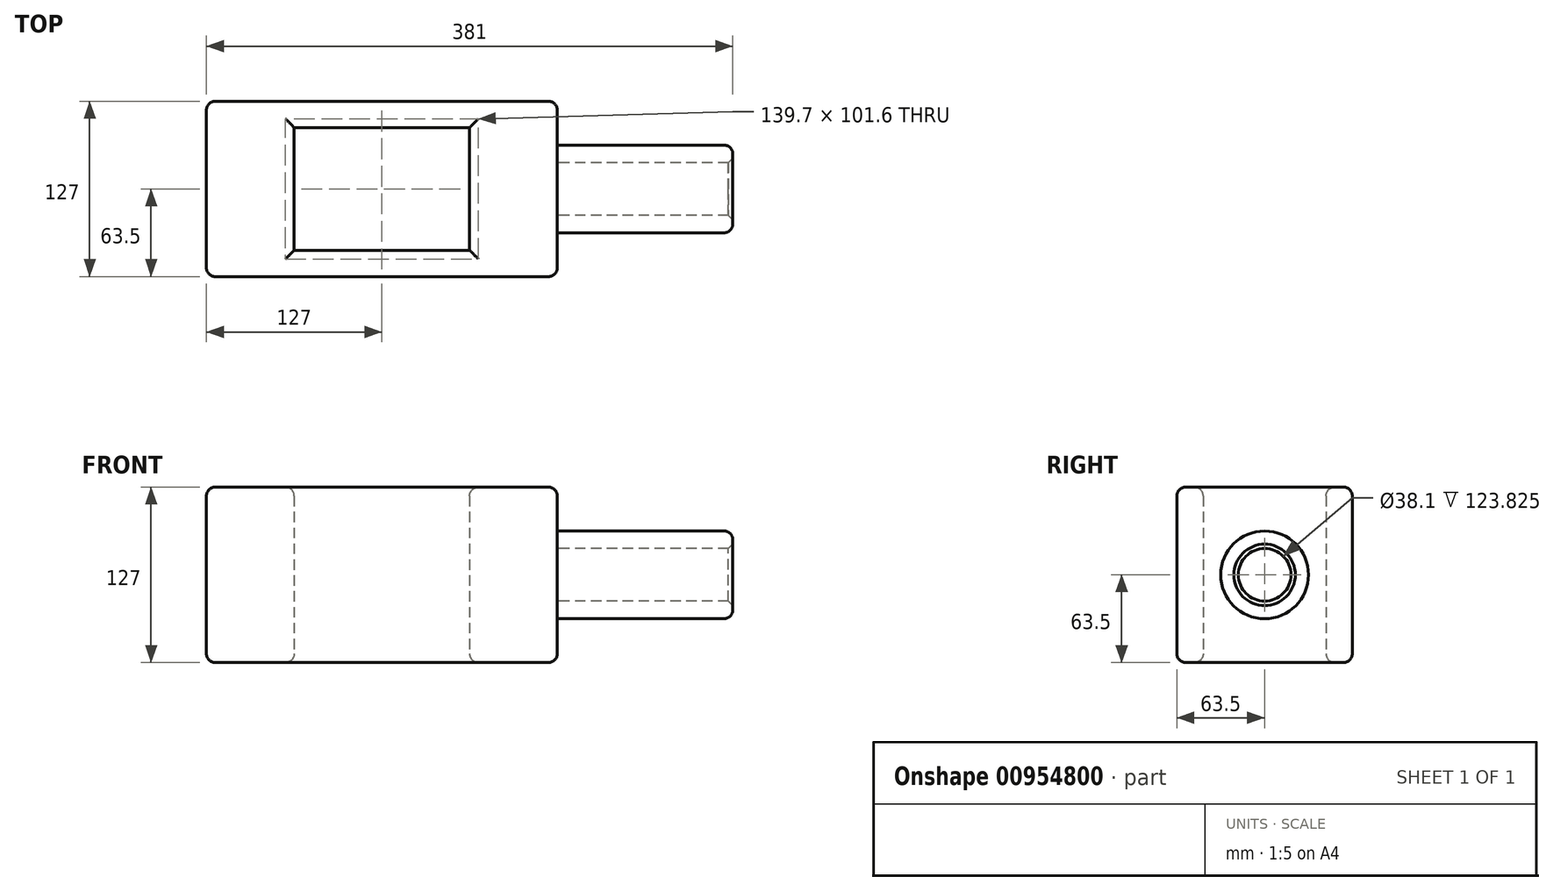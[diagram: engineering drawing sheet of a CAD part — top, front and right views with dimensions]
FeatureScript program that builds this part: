
annotation { "Feature Type Name" : "Feature", "Feature Type Description" : "" }
export const myFeature = defineFeature(function(context is Context, id is Id, definition is map)
    precondition{}
    {
        {
            var Q0;
            Q0=qCreatedBy(makeId("Top.planeOp"),FACE);
            var sketch = newSketch(context, id + "F0", { "sketchPlane" : qUnion([Q0])});
            skLineSegment(sketch, "E0.bottom", {"start": v(127, 63.5) * mm, "end": v(-127, 63.5) * mm});
            skLineSegment(sketch, "E0.top", {"start": v(127, -63.5) * mm, "end": v(-127, -63.5) * mm});
            skLineSegment(sketch, "E0.left", {"start": v(127, 63.5) * mm, "end": v(127, -63.5) * mm});
            skLineSegment(sketch, "E0.right", {"start": v(-127, 63.5) * mm, "end": v(-127, -63.5) * mm});
            skPoint(sketch, "E0.middle", {"position": v(0, 0) * mm});
            skLineSegment(sketch, "E1.bottom", {"start": v(-63.5, -44.45) * mm, "end": v(63.5, -44.45) * mm});
            skLineSegment(sketch, "E1.top", {"start": v(-63.5, 44.45) * mm, "end": v(63.5, 44.45) * mm});
            skLineSegment(sketch, "E1.left", {"start": v(-63.5, -44.45) * mm, "end": v(-63.5, 44.45) * mm});
            skLineSegment(sketch, "E1.right", {"start": v(63.5, -44.45) * mm, "end": v(63.5, 44.45) * mm});
            skSolve(sketch);
        }
        {
            var Q0;
            Q0 = qSketchRegion(id + "F0", true);
            var Q1;
            Q1=makeQuery(id+"F0.imprint","IMPRINT",FACE,{"disambiguationData":[TD([[makeQuery(id+"F0.imprint","IMPRINT",EDGE,{"derivedFrom":sQuery(id+"F0.wireOp",EDGE,"E0.bottom")}),1.0]])]});
            extrude(context, id + "F1", {"entities" : qUnion([Q0, Q1]), "depth" : 127 * mm, "offsetDistance" : 25.4 * mm});
        }
        {
            var Q0;
            Q0=makeQuery(id+"F1.opExtrude","CAP_FACE",FACE,{"disambiguationData":[OSD([sQuery(id+"F0.wireOp",EDGE,"E0.bottom"),sQuery(id+"F0.wireOp",EDGE,"E0.top"),sQuery(id+"F0.wireOp",EDGE,"E0.left"),sQuery(id+"F0.wireOp",EDGE,"E0.right"),sQuery(id+"F0.wireOp",EDGE,"E1.bottom"),sQuery(id+"F0.wireOp",EDGE,"E1.top"),sQuery(id+"F0.wireOp",EDGE,"E1.left"),sQuery(id+"F0.wireOp",EDGE,"E1.right")])],"isStart":false});
            var Q1;
            Q1=makeQuery(id+"F1.opExtrude","CAP_FACE",FACE,{"disambiguationData":[OSD([sQuery(id+"F0.wireOp",EDGE,"E0.bottom"),sQuery(id+"F0.wireOp",EDGE,"E0.top"),sQuery(id+"F0.wireOp",EDGE,"E0.left"),sQuery(id+"F0.wireOp",EDGE,"E0.right"),sQuery(id+"F0.wireOp",EDGE,"E1.bottom"),sQuery(id+"F0.wireOp",EDGE,"E1.top"),sQuery(id+"F0.wireOp",EDGE,"E1.left"),sQuery(id+"F0.wireOp",EDGE,"E1.right")])],"isStart":true});
            var Q2;
            Q2=makeQuery(id+"F1.opExtrude","SWEPT_FACE",FACE,{"disambiguationData":[OSD([sQuery(id+"F0.wireOp",EDGE,"E0.top")])]});
            var Q3;
            Q3=makeQuery(id+"F1.opExtrude","SWEPT_FACE",FACE,{"disambiguationData":[OSD([sQuery(id+"F0.wireOp",EDGE,"E0.bottom")])]});
            fillet(context, id + "F2", {"entities" : qUnion([Q0, Q1, Q2, Q3]), "radius" : 6.35 * mm, "tangentPropagation" : true, "allowEdgeOverflow" : false});
        }
        {
            var Q0;
            Q0=makeQuery(id+"F1.opExtrude","SWEPT_FACE",FACE,{"disambiguationData":[OSD([sQuery(id+"F0.wireOp",EDGE,"E0.left")])]});
            var sketch = newSketch(context, id + "F3", { "sketchPlane" : qUnion([Q0])});
            skCircle(sketch, "E2", {"center": v(0, 63.5) * mm, "radius": 31.75 * mm});
            skPoint(sketch, "E2.centerSnap0", {"position": v(-57.15, 63.5) * mm});
            skCircle(sketch, "E3", {"center": v(0, 63.5) * mm, "radius": 19.05 * mm});
            skSolve(sketch);
        }
        {
            var Q0;
            Q0=makeQuery(id+"F3.imprint","IMPRINT",FACE,{"disambiguationData":[TD([[makeQuery(id+"F3.imprint","IMPRINT",EDGE,{"derivedFrom":sQuery(id+"F3.wireOp",EDGE,"E2")}),1.0]])]});
            extrude(context, id + "F4", {"entities" : qUnion([Q0]), "operationType" : NewBodyOperationType.ADD, "depth" : 127 * mm, "offsetDistance" : 25.4 * mm});
        }
        {
            var Q0;
            Q0=makeQuery(id+"F4.opExtrude","CAP_EDGE",EDGE,{"disambiguationData":[OSD([sQuery(id+"F3.wireOp",EDGE,"E2")])],"isStart":true});
            var Q1;
            Q1=makeQuery(id+"F4.opExtrude","CAP_EDGE",EDGE,{"disambiguationData":[OSD([sQuery(id+"F3.wireOp",EDGE,"E2")])],"isStart":false});
            fillet(context, id + "F5", {"entities" : qUnion([Q0, Q1]), "radius" : 6.35 * mm, "tangentPropagation" : true, "allowEdgeOverflow" : false});
        }
        {
            var Q0;
            Q0=makeQuery(id+"F4.opExtrude","CAP_EDGE",EDGE,{"disambiguationData":[OSD([sQuery(id+"F3.wireOp",EDGE,"E3")])],"isStart":false});
            chamfer(context, id + "F6", {"entities" : qUnion([Q0]), "width" : 3.17 * mm, "tangentPropagation" : true});
        }
    });
